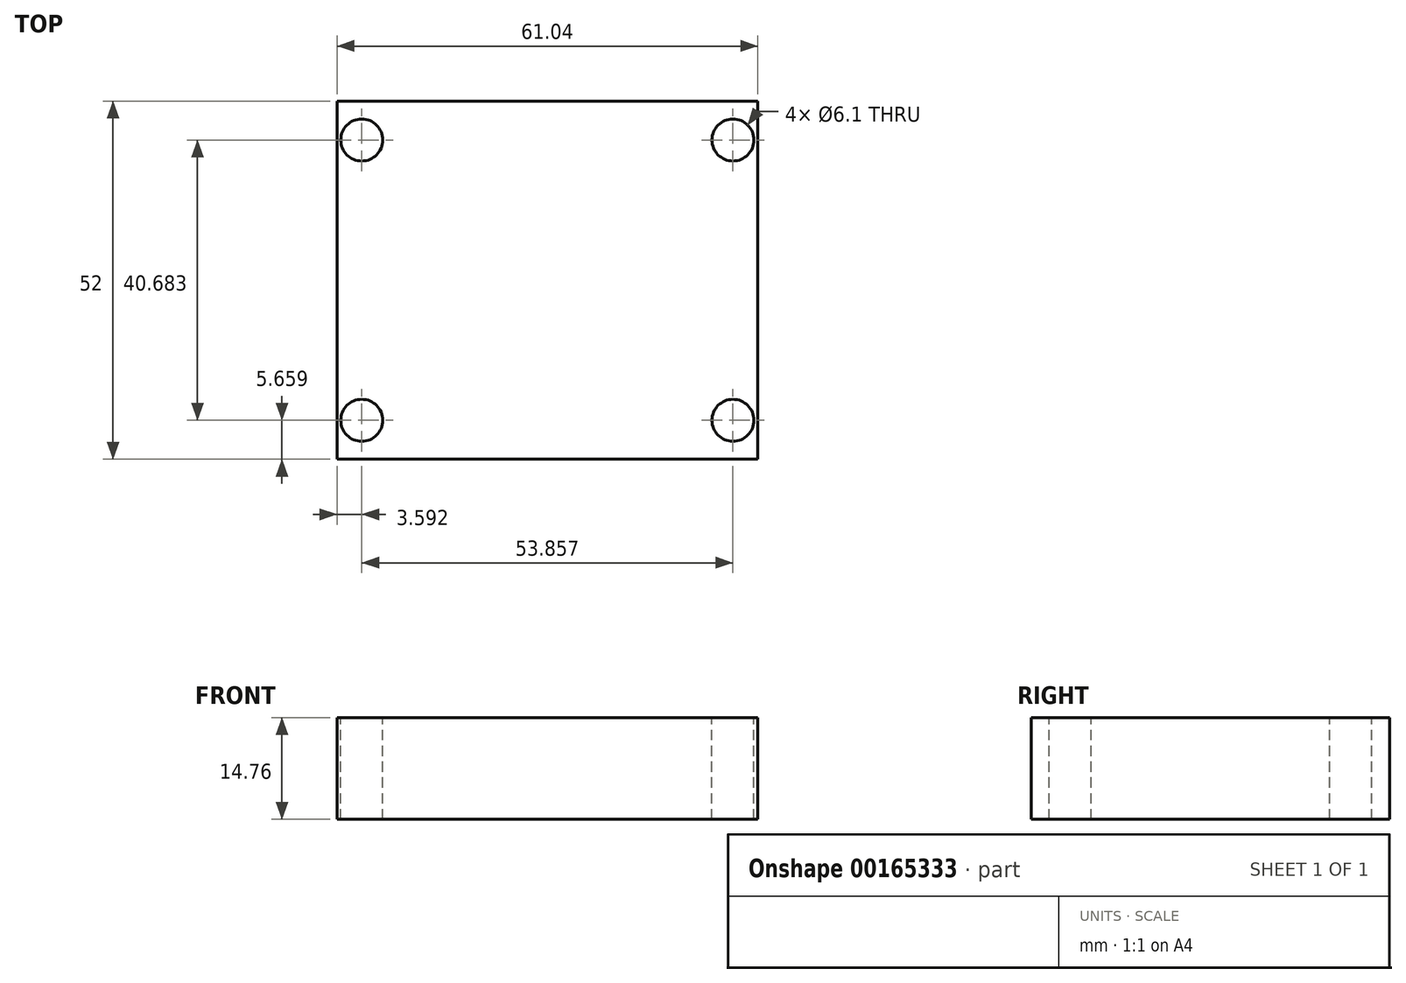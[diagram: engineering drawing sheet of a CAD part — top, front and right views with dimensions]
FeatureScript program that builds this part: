
annotation { "Feature Type Name" : "Feature", "Feature Type Description" : "" }
export const myFeature = defineFeature(function(context is Context, id is Id, definition is map)
    precondition{}
    {
        {
            var Q0;
            Q0=qCreatedBy(makeId("Top.planeOp"),FACE);
            var sketch = newSketch(context, id + "F0", { "sketchPlane" : qUnion([Q0])});
            skLineSegment(sketch, "E0.rect.bottom", {"start": v(30.52, -26) * mm, "end": v(-30.52, -26) * mm});
            skLineSegment(sketch, "E0.rect.top", {"start": v(30.52, 26) * mm, "end": v(-30.52, 26) * mm});
            skLineSegment(sketch, "E0.rect.left", {"start": v(30.52, -26) * mm, "end": v(30.52, 26) * mm});
            skLineSegment(sketch, "E0.rect.right", {"start": v(-30.52, -26) * mm, "end": v(-30.52, 26) * mm});
            skPoint(sketch, "E0.rect.middle", {"position": v(0, 0) * mm});
            skSolve(sketch);
        }
        {
            var Q0;
            Q0=qSketchRegion(id+"F0",true);
            extrude(context, id + "F1", {"entities" : qUnion([Q0]), "depth" : 14.76 * mm});
        }
        {
            var Q0;
            Q0=makeQuery(id+"F1.opExtrude","CAP_FACE",FACE,{"disambiguationData":[OSD([sQuery(id+"F0.wireOp",EDGE,"E0.rect.bottom"),sQuery(id+"F0.wireOp",EDGE,"E0.rect.top"),sQuery(id+"F0.wireOp",EDGE,"E0.rect.left"),sQuery(id+"F0.wireOp",EDGE,"E0.rect.right")])],"isStart":false});
            var sketch = newSketch(context, id + "F2", { "sketchPlane" : qUnion([Q0])});
            skPoint(sketch, "E1.rect.middle", {"position": v(0, 0) * mm});
            skCircle(sketch, "E2", {"center": v(-26.93, 20.34) * mm, "radius": 3.05 * mm});
            skCircle(sketch, "E3", {"center": v(26.93, 20.34) * mm, "radius": 3.05 * mm});
            skCircle(sketch, "E4", {"center": v(26.93, -20.34) * mm, "radius": 3.05 * mm});
            skCircle(sketch, "E5", {"center": v(-26.93, -20.34) * mm, "radius": 3.05 * mm});
            skSolve(sketch);
        }
        {
            var Q0;
            Q0=qSketchRegion(id+"F2",true);
            extrude(context, id + "F3", {"entities" : qUnion([Q0]), "operationType" : NewBodyOperationType.REMOVE, "endBound" : BoundingType.THROUGH_ALL, "oppositeDirection" : true, "depth" : 25.4 * mm});
        }
    });
